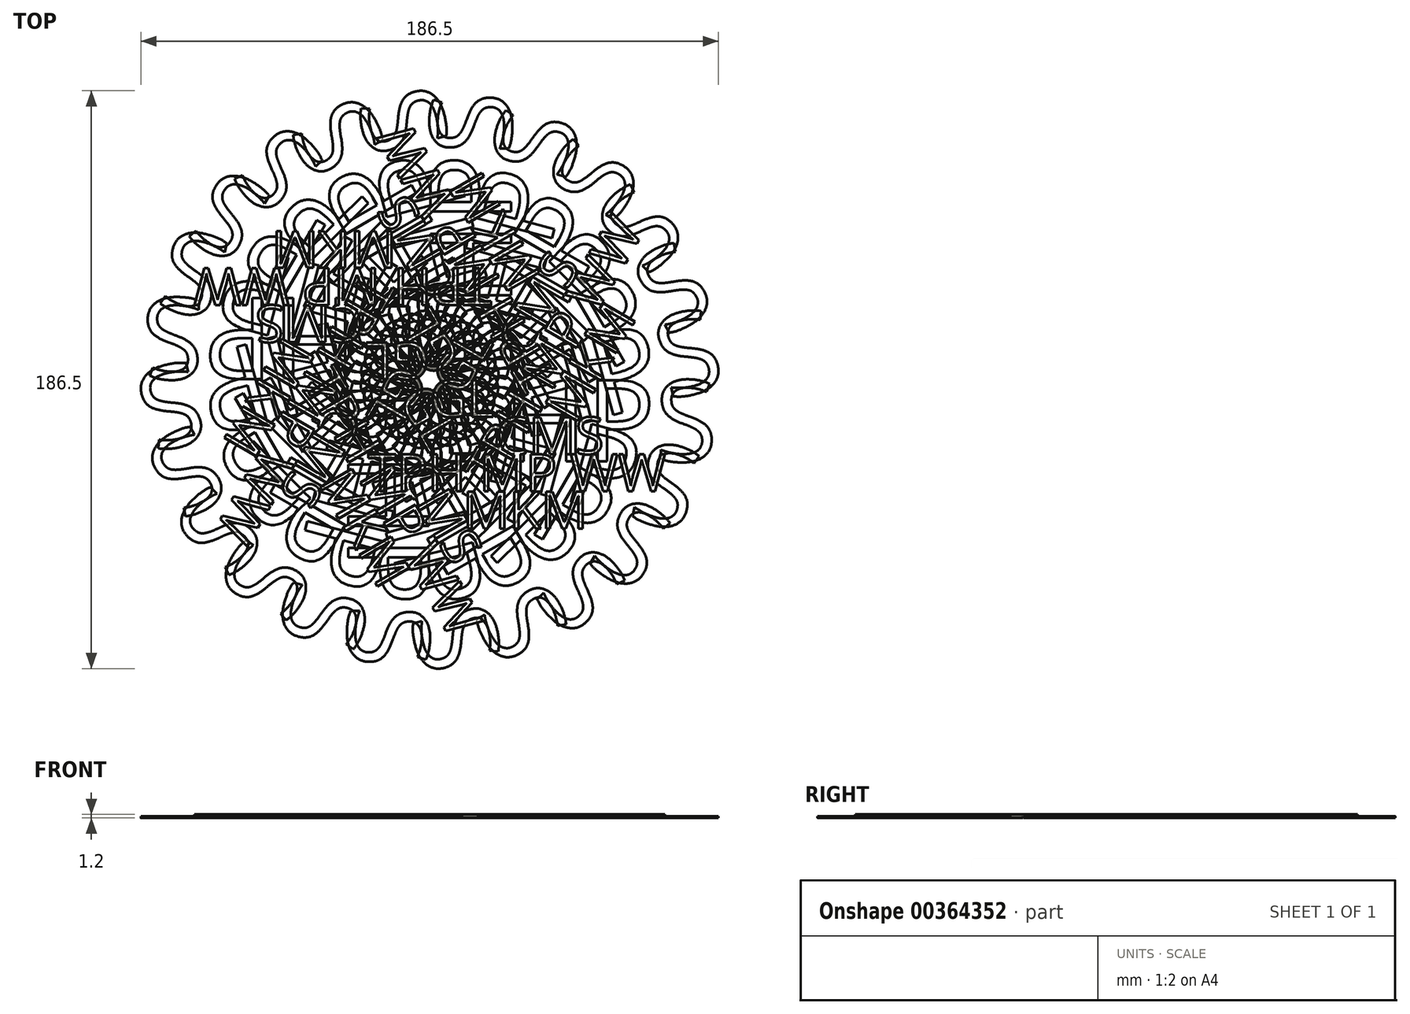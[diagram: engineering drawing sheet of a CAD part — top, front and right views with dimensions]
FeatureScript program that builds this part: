
annotation { "Feature Type Name" : "Feature", "Feature Type Description" : "" }
export const myFeature = defineFeature(function(context is Context, id is Id, definition is map)
    precondition{}
    {
        {
            var Q0;
            Q0=qCreatedBy(makeId("Top.planeOp"),FACE);
            var sketch = newSketch(context, id + "F0", { "sketchPlane" : qUnion([Q0])});
            skText(sketch, "E0", { "text": "GL", "fontName": "OpenSans-Regular.ttf"});
            skText(sketch, "E1", { "text": "CMS", "fontName": "OpenSans-Regular.ttf"});
            skText(sketch, "E2", { "text": "TPH MP WW", "fontName": "OpenSans-Regular.ttf"});
            skText(sketch, "E3", { "text": "MKM", "fontName": "OpenSans-Regular.ttf"});
            const initialGuessF0  = {"E0": [0, -0.012, 1, 0, 0.012], "E1": [0.02148, -0.024, 1, 0, 0.012], "E2": [-0.01992, -0.036, 1, 0, 0.012], "E3": [0.01068, -0.048, 1, 0, 0.012]};
            skSetInitialGuess(sketch, initialGuessF0);
            skSolve(sketch);
        }
        {
            var Q0;
            Q0 = qSketchRegion(id + "F0", true);
            extrude(context, id + "F1", {"entities" : qUnion([Q0]), "depth" : 1.2 * mm});
        }
        {
            var Q0;
            Q0=qCreatedBy(makeId("Front.planeOp"),FACE);
            var sketch = newSketch(context, id + "F2", { "sketchPlane" : qUnion([Q0])});
            skLineSegment(sketch, "E4", {"start": v(0, 0) * mm, "end": v(0, 31.4) * mm, "construction": true});
            skSolve(sketch);
        }
        {
            var Q0;
            Q0=makeQuery(id+"F1.opExtrude","SWEPT_BODY",BODY,{"disambiguationData":[OSD([sQuery(id+"F0.wireOp",EDGE,"E0.sketch_text.stroke-0"),sQuery(id+"F0.wireOp",EDGE,"E0.sketch_text.stroke-1"),sQuery(id+"F0.wireOp",EDGE,"E0.sketch_text.stroke-2"),sQuery(id+"F0.wireOp",EDGE,"E0.sketch_text.stroke-3"),sQuery(id+"F0.wireOp",EDGE,"E0.sketch_text.stroke-4"),sQuery(id+"F0.wireOp",EDGE,"E0.sketch_text.stroke-5"),sQuery(id+"F0.wireOp",EDGE,"E0.sketch_text.stroke-6"),sQuery(id+"F0.wireOp",EDGE,"E0.sketch_text.stroke-7"),sQuery(id+"F0.wireOp",EDGE,"E0.sketch_text.stroke-8"),sQuery(id+"F0.wireOp",EDGE,"E0.sketch_text.stroke-9"),sQuery(id+"F0.wireOp",EDGE,"E0.sketch_text.stroke-10"),sQuery(id+"F0.wireOp",EDGE,"E0.sketch_text.stroke-11"),sQuery(id+"F0.wireOp",EDGE,"E0.sketch_text.stroke-12"),sQuery(id+"F0.wireOp",EDGE,"E0.sketch_text.stroke-13"),sQuery(id+"F0.wireOp",EDGE,"E0.sketch_text.stroke-14"),sQuery(id+"F0.wireOp",EDGE,"E0.sketch_text.stroke-15"),sQuery(id+"F0.wireOp",EDGE,"E0.sketch_text.stroke-16"),sQuery(id+"F0.wireOp",EDGE,"E0.sketch_text.stroke-17"),sQuery(id+"F0.wireOp",EDGE,"E0.sketch_text.stroke-18"),sQuery(id+"F0.wireOp",EDGE,"E0.sketch_text.stroke-19")])]});
            var Q1;
            Q1=makeQuery(id+"F1.opExtrude","SWEPT_BODY",BODY,{"disambiguationData":[OSD([sQuery(id+"F0.wireOp",EDGE,"E1.sketch_text.stroke-0"),sQuery(id+"F0.wireOp",EDGE,"E1.sketch_text.stroke-1"),sQuery(id+"F0.wireOp",EDGE,"E1.sketch_text.stroke-2"),sQuery(id+"F0.wireOp",EDGE,"E1.sketch_text.stroke-3"),sQuery(id+"F0.wireOp",EDGE,"E1.sketch_text.stroke-4"),sQuery(id+"F0.wireOp",EDGE,"E1.sketch_text.stroke-5"),sQuery(id+"F0.wireOp",EDGE,"E1.sketch_text.stroke-6"),sQuery(id+"F0.wireOp",EDGE,"E1.sketch_text.stroke-7"),sQuery(id+"F0.wireOp",EDGE,"E1.sketch_text.stroke-8"),sQuery(id+"F0.wireOp",EDGE,"E1.sketch_text.stroke-9"),sQuery(id+"F0.wireOp",EDGE,"E1.sketch_text.stroke-10"),sQuery(id+"F0.wireOp",EDGE,"E1.sketch_text.stroke-11"),sQuery(id+"F0.wireOp",EDGE,"E1.sketch_text.stroke-12"),sQuery(id+"F0.wireOp",EDGE,"E1.sketch_text.stroke-13"),sQuery(id+"F0.wireOp",EDGE,"E1.sketch_text.stroke-14"),sQuery(id+"F0.wireOp",EDGE,"E2.sketch_text.stroke-35"),sQuery(id+"F0.wireOp",EDGE,"E2.sketch_text.stroke-36"),sQuery(id+"F0.wireOp",EDGE,"E2.sketch_text.stroke-37"),sQuery(id+"F0.wireOp",EDGE,"E2.sketch_text.stroke-38"),sQuery(id+"F0.wireOp",EDGE,"E2.sketch_text.stroke-39"),sQuery(id+"F0.wireOp",EDGE,"E2.sketch_text.stroke-40"),sQuery(id+"F0.wireOp",EDGE,"E2.sketch_text.stroke-41"),sQuery(id+"F0.wireOp",EDGE,"E2.sketch_text.stroke-42"),sQuery(id+"F0.wireOp",EDGE,"E2.sketch_text.stroke-43"),sQuery(id+"F0.wireOp",EDGE,"E2.sketch_text.stroke-44"),sQuery(id+"F0.wireOp",EDGE,"E2.sketch_text.stroke-45"),sQuery(id+"F0.wireOp",EDGE,"E2.sketch_text.stroke-46"),sQuery(id+"F0.wireOp",EDGE,"E2.sketch_text.stroke-47"),sQuery(id+"F0.wireOp",EDGE,"E2.sketch_text.stroke-48"),sQuery(id+"F0.wireOp",EDGE,"E2.sketch_text.stroke-49"),sQuery(id+"F0.wireOp",EDGE,"E2.sketch_text.stroke-50"),sQuery(id+"F0.wireOp",EDGE,"E2.sketch_text.stroke-51"),sQuery(id+"F0.wireOp",EDGE,"E2.sketch_text.stroke-52")])]});
            var Q2;
            Q2=makeQuery(id+"F1.opExtrude","SWEPT_BODY",BODY,{"disambiguationData":[OSD([sQuery(id+"F0.wireOp",EDGE,"E0.sketch_text.stroke-20"),sQuery(id+"F0.wireOp",EDGE,"E0.sketch_text.stroke-21"),sQuery(id+"F0.wireOp",EDGE,"E0.sketch_text.stroke-22"),sQuery(id+"F0.wireOp",EDGE,"E0.sketch_text.stroke-23"),sQuery(id+"F0.wireOp",EDGE,"E0.sketch_text.stroke-24"),sQuery(id+"F0.wireOp",EDGE,"E0.sketch_text.stroke-25")])]});
            var Q3;
            Q3=makeQuery(id+"F1.opExtrude","SWEPT_BODY",BODY,{"disambiguationData":[OSD([sQuery(id+"F0.wireOp",EDGE,"E1.sketch_text.stroke-15"),sQuery(id+"F0.wireOp",EDGE,"E1.sketch_text.stroke-16"),sQuery(id+"F0.wireOp",EDGE,"E1.sketch_text.stroke-17"),sQuery(id+"F0.wireOp",EDGE,"E1.sketch_text.stroke-18"),sQuery(id+"F0.wireOp",EDGE,"E1.sketch_text.stroke-19"),sQuery(id+"F0.wireOp",EDGE,"E1.sketch_text.stroke-20"),sQuery(id+"F0.wireOp",EDGE,"E1.sketch_text.stroke-21"),sQuery(id+"F0.wireOp",EDGE,"E1.sketch_text.stroke-22"),sQuery(id+"F0.wireOp",EDGE,"E1.sketch_text.stroke-23"),sQuery(id+"F0.wireOp",EDGE,"E1.sketch_text.stroke-24"),sQuery(id+"F0.wireOp",EDGE,"E1.sketch_text.stroke-25"),sQuery(id+"F0.wireOp",EDGE,"E1.sketch_text.stroke-26"),sQuery(id+"F0.wireOp",EDGE,"E1.sketch_text.stroke-27"),sQuery(id+"F0.wireOp",EDGE,"E1.sketch_text.stroke-28"),sQuery(id+"F0.wireOp",EDGE,"E1.sketch_text.stroke-29"),sQuery(id+"F0.wireOp",EDGE,"E1.sketch_text.stroke-30"),sQuery(id+"F0.wireOp",EDGE,"E1.sketch_text.stroke-31"),sQuery(id+"F0.wireOp",EDGE,"E1.sketch_text.stroke-32")])]});
            var Q4;
            Q4=makeQuery(id+"F1.opExtrude","SWEPT_BODY",BODY,{"disambiguationData":[OSD([sQuery(id+"F0.wireOp",EDGE,"E2.sketch_text.stroke-0"),sQuery(id+"F0.wireOp",EDGE,"E2.sketch_text.stroke-1"),sQuery(id+"F0.wireOp",EDGE,"E2.sketch_text.stroke-2"),sQuery(id+"F0.wireOp",EDGE,"E2.sketch_text.stroke-3"),sQuery(id+"F0.wireOp",EDGE,"E2.sketch_text.stroke-4"),sQuery(id+"F0.wireOp",EDGE,"E2.sketch_text.stroke-5"),sQuery(id+"F0.wireOp",EDGE,"E2.sketch_text.stroke-6"),sQuery(id+"F0.wireOp",EDGE,"E2.sketch_text.stroke-7")])]});
            var Q5;
            Q5=makeQuery(id+"F1.opExtrude","SWEPT_BODY",BODY,{"disambiguationData":[OSD([sQuery(id+"F0.wireOp",EDGE,"E1.sketch_text.stroke-33"),sQuery(id+"F0.wireOp",EDGE,"E1.sketch_text.stroke-34"),sQuery(id+"F0.wireOp",EDGE,"E1.sketch_text.stroke-35"),sQuery(id+"F0.wireOp",EDGE,"E1.sketch_text.stroke-36"),sQuery(id+"F0.wireOp",EDGE,"E1.sketch_text.stroke-37"),sQuery(id+"F0.wireOp",EDGE,"E1.sketch_text.stroke-38"),sQuery(id+"F0.wireOp",EDGE,"E1.sketch_text.stroke-39"),sQuery(id+"F0.wireOp",EDGE,"E1.sketch_text.stroke-40"),sQuery(id+"F0.wireOp",EDGE,"E1.sketch_text.stroke-41"),sQuery(id+"F0.wireOp",EDGE,"E1.sketch_text.stroke-42"),sQuery(id+"F0.wireOp",EDGE,"E1.sketch_text.stroke-43"),sQuery(id+"F0.wireOp",EDGE,"E1.sketch_text.stroke-44"),sQuery(id+"F0.wireOp",EDGE,"E1.sketch_text.stroke-45"),sQuery(id+"F0.wireOp",EDGE,"E1.sketch_text.stroke-46"),sQuery(id+"F0.wireOp",EDGE,"E1.sketch_text.stroke-47"),sQuery(id+"F0.wireOp",EDGE,"E1.sketch_text.stroke-48"),sQuery(id+"F0.wireOp",EDGE,"E1.sketch_text.stroke-49"),sQuery(id+"F0.wireOp",EDGE,"E1.sketch_text.stroke-50"),sQuery(id+"F0.wireOp",EDGE,"E1.sketch_text.stroke-51"),sQuery(id+"F0.wireOp",EDGE,"E1.sketch_text.stroke-52"),sQuery(id+"F0.wireOp",EDGE,"E1.sketch_text.stroke-53"),sQuery(id+"F0.wireOp",EDGE,"E1.sketch_text.stroke-54"),sQuery(id+"F0.wireOp",EDGE,"E1.sketch_text.stroke-55"),sQuery(id+"F0.wireOp",EDGE,"E1.sketch_text.stroke-56"),sQuery(id+"F0.wireOp",EDGE,"E1.sketch_text.stroke-57")])]});
            var Q6;
            Q6=makeQuery(id+"F1.opExtrude","SWEPT_BODY",BODY,{"disambiguationData":[OSD([sQuery(id+"F0.wireOp",EDGE,"E2.sketch_text.stroke-8"),sQuery(id+"F0.wireOp",EDGE,"E2.sketch_text.stroke-9"),sQuery(id+"F0.wireOp",EDGE,"E2.sketch_text.stroke-10"),sQuery(id+"F0.wireOp",EDGE,"E2.sketch_text.stroke-11"),sQuery(id+"F0.wireOp",EDGE,"E2.sketch_text.stroke-12"),sQuery(id+"F0.wireOp",EDGE,"E2.sketch_text.stroke-13"),sQuery(id+"F0.wireOp",EDGE,"E2.sketch_text.stroke-14"),sQuery(id+"F0.wireOp",EDGE,"E2.sketch_text.stroke-15"),sQuery(id+"F0.wireOp",EDGE,"E2.sketch_text.stroke-16"),sQuery(id+"F0.wireOp",EDGE,"E2.sketch_text.stroke-17"),sQuery(id+"F0.wireOp",EDGE,"E2.sketch_text.stroke-18"),sQuery(id+"F0.wireOp",EDGE,"E2.sketch_text.stroke-19"),sQuery(id+"F0.wireOp",EDGE,"E2.sketch_text.stroke-20"),sQuery(id+"F0.wireOp",EDGE,"E2.sketch_text.stroke-21"),sQuery(id+"F0.wireOp",EDGE,"E2.sketch_text.stroke-22")])]});
            var Q7;
            Q7=makeQuery(id+"F1.opExtrude","SWEPT_BODY",BODY,{"disambiguationData":[OSD([sQuery(id+"F0.wireOp",EDGE,"E2.sketch_text.stroke-23"),sQuery(id+"F0.wireOp",EDGE,"E2.sketch_text.stroke-24"),sQuery(id+"F0.wireOp",EDGE,"E2.sketch_text.stroke-25"),sQuery(id+"F0.wireOp",EDGE,"E2.sketch_text.stroke-26"),sQuery(id+"F0.wireOp",EDGE,"E2.sketch_text.stroke-27"),sQuery(id+"F0.wireOp",EDGE,"E2.sketch_text.stroke-28"),sQuery(id+"F0.wireOp",EDGE,"E2.sketch_text.stroke-29"),sQuery(id+"F0.wireOp",EDGE,"E2.sketch_text.stroke-30"),sQuery(id+"F0.wireOp",EDGE,"E2.sketch_text.stroke-31"),sQuery(id+"F0.wireOp",EDGE,"E2.sketch_text.stroke-32"),sQuery(id+"F0.wireOp",EDGE,"E2.sketch_text.stroke-33"),sQuery(id+"F0.wireOp",EDGE,"E2.sketch_text.stroke-34")])]});
            var Q8;
            Q8=makeQuery(id+"F1.opExtrude","SWEPT_BODY",BODY,{"disambiguationData":[OSD([sQuery(id+"F0.wireOp",EDGE,"E2.sketch_text.stroke-53"),sQuery(id+"F0.wireOp",EDGE,"E2.sketch_text.stroke-54"),sQuery(id+"F0.wireOp",EDGE,"E2.sketch_text.stroke-55"),sQuery(id+"F0.wireOp",EDGE,"E2.sketch_text.stroke-56"),sQuery(id+"F0.wireOp",EDGE,"E2.sketch_text.stroke-57"),sQuery(id+"F0.wireOp",EDGE,"E2.sketch_text.stroke-58"),sQuery(id+"F0.wireOp",EDGE,"E2.sketch_text.stroke-59"),sQuery(id+"F0.wireOp",EDGE,"E2.sketch_text.stroke-60"),sQuery(id+"F0.wireOp",EDGE,"E2.sketch_text.stroke-61"),sQuery(id+"F0.wireOp",EDGE,"E2.sketch_text.stroke-62"),sQuery(id+"F0.wireOp",EDGE,"E2.sketch_text.stroke-63"),sQuery(id+"F0.wireOp",EDGE,"E2.sketch_text.stroke-64"),sQuery(id+"F0.wireOp",EDGE,"E2.sketch_text.stroke-65"),sQuery(id+"F0.wireOp",EDGE,"E2.sketch_text.stroke-66"),sQuery(id+"F0.wireOp",EDGE,"E2.sketch_text.stroke-67")])]});
            var Q9;
            Q9=makeQuery(id+"F1.opExtrude","SWEPT_BODY",BODY,{"disambiguationData":[OSD([sQuery(id+"F0.wireOp",EDGE,"E3.sketch_text.stroke-18"),sQuery(id+"F0.wireOp",EDGE,"E3.sketch_text.stroke-19"),sQuery(id+"F0.wireOp",EDGE,"E3.sketch_text.stroke-20"),sQuery(id+"F0.wireOp",EDGE,"E3.sketch_text.stroke-21"),sQuery(id+"F0.wireOp",EDGE,"E3.sketch_text.stroke-22"),sQuery(id+"F0.wireOp",EDGE,"E3.sketch_text.stroke-23"),sQuery(id+"F0.wireOp",EDGE,"E3.sketch_text.stroke-24"),sQuery(id+"F0.wireOp",EDGE,"E3.sketch_text.stroke-25"),sQuery(id+"F0.wireOp",EDGE,"E3.sketch_text.stroke-26"),sQuery(id+"F0.wireOp",EDGE,"E3.sketch_text.stroke-27"),sQuery(id+"F0.wireOp",EDGE,"E3.sketch_text.stroke-28"),sQuery(id+"F0.wireOp",EDGE,"E3.sketch_text.stroke-29")])]});
            var Q10;
            Q10=makeQuery(id+"F1.opExtrude","SWEPT_BODY",BODY,{"disambiguationData":[OSD([sQuery(id+"F0.wireOp",EDGE,"E3.sketch_text.stroke-0"),sQuery(id+"F0.wireOp",EDGE,"E3.sketch_text.stroke-1"),sQuery(id+"F0.wireOp",EDGE,"E3.sketch_text.stroke-2"),sQuery(id+"F0.wireOp",EDGE,"E3.sketch_text.stroke-3"),sQuery(id+"F0.wireOp",EDGE,"E3.sketch_text.stroke-4"),sQuery(id+"F0.wireOp",EDGE,"E3.sketch_text.stroke-5"),sQuery(id+"F0.wireOp",EDGE,"E3.sketch_text.stroke-6"),sQuery(id+"F0.wireOp",EDGE,"E3.sketch_text.stroke-7"),sQuery(id+"F0.wireOp",EDGE,"E3.sketch_text.stroke-8"),sQuery(id+"F0.wireOp",EDGE,"E3.sketch_text.stroke-9"),sQuery(id+"F0.wireOp",EDGE,"E3.sketch_text.stroke-10"),sQuery(id+"F0.wireOp",EDGE,"E3.sketch_text.stroke-11"),sQuery(id+"F0.wireOp",EDGE,"E3.sketch_text.stroke-12"),sQuery(id+"F0.wireOp",EDGE,"E3.sketch_text.stroke-13"),sQuery(id+"F0.wireOp",EDGE,"E3.sketch_text.stroke-14"),sQuery(id+"F0.wireOp",EDGE,"E3.sketch_text.stroke-15"),sQuery(id+"F0.wireOp",EDGE,"E3.sketch_text.stroke-16"),sQuery(id+"F0.wireOp",EDGE,"E3.sketch_text.stroke-17")])]});
            var Q11;
            Q11=makeQuery(id+"F1.opExtrude","SWEPT_BODY",BODY,{"disambiguationData":[OSD([sQuery(id+"F0.wireOp",EDGE,"E2.sketch_text.stroke-88"),sQuery(id+"F0.wireOp",EDGE,"E2.sketch_text.stroke-89"),sQuery(id+"F0.wireOp",EDGE,"E2.sketch_text.stroke-90"),sQuery(id+"F0.wireOp",EDGE,"E2.sketch_text.stroke-91"),sQuery(id+"F0.wireOp",EDGE,"E2.sketch_text.stroke-92"),sQuery(id+"F0.wireOp",EDGE,"E2.sketch_text.stroke-93"),sQuery(id+"F0.wireOp",EDGE,"E2.sketch_text.stroke-94"),sQuery(id+"F0.wireOp",EDGE,"E2.sketch_text.stroke-95"),sQuery(id+"F0.wireOp",EDGE,"E2.sketch_text.stroke-96"),sQuery(id+"F0.wireOp",EDGE,"E2.sketch_text.stroke-97"),sQuery(id+"F0.wireOp",EDGE,"E2.sketch_text.stroke-98"),sQuery(id+"F0.wireOp",EDGE,"E2.sketch_text.stroke-99"),sQuery(id+"F0.wireOp",EDGE,"E2.sketch_text.stroke-100"),sQuery(id+"F0.wireOp",EDGE,"E2.sketch_text.stroke-101"),sQuery(id+"F0.wireOp",EDGE,"E2.sketch_text.stroke-102"),sQuery(id+"F0.wireOp",EDGE,"E2.sketch_text.stroke-103"),sQuery(id+"F0.wireOp",EDGE,"E2.sketch_text.stroke-104"),sQuery(id+"F0.wireOp",EDGE,"E2.sketch_text.stroke-105"),sQuery(id+"F0.wireOp",EDGE,"E2.sketch_text.stroke-106"),sQuery(id+"F0.wireOp",EDGE,"E2.sketch_text.stroke-107")])]});
            var Q12;
            Q12=makeQuery(id+"F1.opExtrude","SWEPT_BODY",BODY,{"disambiguationData":[OSD([sQuery(id+"F0.wireOp",EDGE,"E2.sketch_text.stroke-68"),sQuery(id+"F0.wireOp",EDGE,"E2.sketch_text.stroke-69"),sQuery(id+"F0.wireOp",EDGE,"E2.sketch_text.stroke-70"),sQuery(id+"F0.wireOp",EDGE,"E2.sketch_text.stroke-71"),sQuery(id+"F0.wireOp",EDGE,"E2.sketch_text.stroke-72"),sQuery(id+"F0.wireOp",EDGE,"E2.sketch_text.stroke-73"),sQuery(id+"F0.wireOp",EDGE,"E2.sketch_text.stroke-74"),sQuery(id+"F0.wireOp",EDGE,"E2.sketch_text.stroke-75"),sQuery(id+"F0.wireOp",EDGE,"E2.sketch_text.stroke-76"),sQuery(id+"F0.wireOp",EDGE,"E2.sketch_text.stroke-77"),sQuery(id+"F0.wireOp",EDGE,"E2.sketch_text.stroke-78"),sQuery(id+"F0.wireOp",EDGE,"E2.sketch_text.stroke-79"),sQuery(id+"F0.wireOp",EDGE,"E2.sketch_text.stroke-80"),sQuery(id+"F0.wireOp",EDGE,"E2.sketch_text.stroke-81"),sQuery(id+"F0.wireOp",EDGE,"E2.sketch_text.stroke-82"),sQuery(id+"F0.wireOp",EDGE,"E2.sketch_text.stroke-83"),sQuery(id+"F0.wireOp",EDGE,"E2.sketch_text.stroke-84"),sQuery(id+"F0.wireOp",EDGE,"E2.sketch_text.stroke-85"),sQuery(id+"F0.wireOp",EDGE,"E2.sketch_text.stroke-86"),sQuery(id+"F0.wireOp",EDGE,"E2.sketch_text.stroke-87")])]});
            var Q13;
            Q13=makeQuery(id+"F1.opExtrude","SWEPT_BODY",BODY,{"disambiguationData":[OSD([sQuery(id+"F0.wireOp",EDGE,"E3.sketch_text.stroke-30"),sQuery(id+"F0.wireOp",EDGE,"E3.sketch_text.stroke-31"),sQuery(id+"F0.wireOp",EDGE,"E3.sketch_text.stroke-32"),sQuery(id+"F0.wireOp",EDGE,"E3.sketch_text.stroke-33"),sQuery(id+"F0.wireOp",EDGE,"E3.sketch_text.stroke-34"),sQuery(id+"F0.wireOp",EDGE,"E3.sketch_text.stroke-35"),sQuery(id+"F0.wireOp",EDGE,"E3.sketch_text.stroke-36"),sQuery(id+"F0.wireOp",EDGE,"E3.sketch_text.stroke-37"),sQuery(id+"F0.wireOp",EDGE,"E3.sketch_text.stroke-38"),sQuery(id+"F0.wireOp",EDGE,"E3.sketch_text.stroke-39"),sQuery(id+"F0.wireOp",EDGE,"E3.sketch_text.stroke-40"),sQuery(id+"F0.wireOp",EDGE,"E3.sketch_text.stroke-41"),sQuery(id+"F0.wireOp",EDGE,"E3.sketch_text.stroke-42"),sQuery(id+"F0.wireOp",EDGE,"E3.sketch_text.stroke-43"),sQuery(id+"F0.wireOp",EDGE,"E3.sketch_text.stroke-44"),sQuery(id+"F0.wireOp",EDGE,"E3.sketch_text.stroke-45"),sQuery(id+"F0.wireOp",EDGE,"E3.sketch_text.stroke-46"),sQuery(id+"F0.wireOp",EDGE,"E3.sketch_text.stroke-47")])]});
            var Q14;
            Q14=sQuery(id+"F2.wireOp",EDGE,"E4");
            circularPattern(context, id + "F3", {"entities" : qUnion([Q0, Q1, Q2, Q3, Q4, Q5, Q6, Q7, Q8, Q9, Q10, Q11, Q12, Q13]), "axis" : qUnion([Q14]), "angle" : 360 * degree, "instanceCount" : 6, "oppositeDirection" : true, "equalSpace" : true});
        }
        {
            var Q0;
            Q0=qCreatedBy(makeId("Top.planeOp"),FACE);
            var sketch = newSketch(context, id + "F4", { "sketchPlane" : qUnion([Q0])});
            skText(sketch, "E5", { "text": "BHPS", "fontName": "OpenSans-Regular.ttf"});
            const initialGuessF4  = {"E5": [0, -0.02634, 1, 0, 0.02634]};
            skSetInitialGuess(sketch, initialGuessF4);
            skSolve(sketch);
        }
        {
            var Q0;
            Q0 = qSketchRegion(id + "F4", true);
            extrude(context, id + "F5", {"entities" : qUnion([Q0]), "depth" : .6 * mm});
        }
        {
            var Q0;
            Q0=makeQuery(id+"F5.opExtrude","SWEPT_BODY",BODY,{"disambiguationData":[OSD([sQuery(id+"F4.wireOp",EDGE,"E5.sketch_text.stroke-0"),sQuery(id+"F4.wireOp",EDGE,"E5.sketch_text.stroke-1"),sQuery(id+"F4.wireOp",EDGE,"E5.sketch_text.stroke-2"),sQuery(id+"F4.wireOp",EDGE,"E5.sketch_text.stroke-3"),sQuery(id+"F4.wireOp",EDGE,"E5.sketch_text.stroke-4"),sQuery(id+"F4.wireOp",EDGE,"E5.sketch_text.stroke-5"),sQuery(id+"F4.wireOp",EDGE,"E5.sketch_text.stroke-6"),sQuery(id+"F4.wireOp",EDGE,"E5.sketch_text.stroke-7"),sQuery(id+"F4.wireOp",EDGE,"E5.sketch_text.stroke-8"),sQuery(id+"F4.wireOp",EDGE,"E5.sketch_text.stroke-9"),sQuery(id+"F4.wireOp",EDGE,"E5.sketch_text.stroke-10"),sQuery(id+"F4.wireOp",EDGE,"E5.sketch_text.stroke-11"),sQuery(id+"F4.wireOp",EDGE,"E5.sketch_text.stroke-12"),sQuery(id+"F4.wireOp",EDGE,"E5.sketch_text.stroke-13"),sQuery(id+"F4.wireOp",EDGE,"E5.sketch_text.stroke-14"),sQuery(id+"F4.wireOp",EDGE,"E5.sketch_text.stroke-15"),sQuery(id+"F4.wireOp",EDGE,"E5.sketch_text.stroke-16"),sQuery(id+"F4.wireOp",EDGE,"E5.sketch_text.stroke-17"),sQuery(id+"F4.wireOp",EDGE,"E5.sketch_text.stroke-18"),sQuery(id+"F4.wireOp",EDGE,"E5.sketch_text.stroke-19"),sQuery(id+"F4.wireOp",EDGE,"E5.sketch_text.stroke-20"),sQuery(id+"F4.wireOp",EDGE,"E5.sketch_text.stroke-21"),sQuery(id+"F4.wireOp",EDGE,"E5.sketch_text.stroke-22"),sQuery(id+"F4.wireOp",EDGE,"E5.sketch_text.stroke-23"),sQuery(id+"F4.wireOp",EDGE,"E5.sketch_text.stroke-24")])]});
            var Q1;
            Q1=makeQuery(id+"F5.opExtrude","SWEPT_BODY",BODY,{"disambiguationData":[OSD([sQuery(id+"F4.wireOp",EDGE,"E5.sketch_text.stroke-25"),sQuery(id+"F4.wireOp",EDGE,"E5.sketch_text.stroke-26"),sQuery(id+"F4.wireOp",EDGE,"E5.sketch_text.stroke-27"),sQuery(id+"F4.wireOp",EDGE,"E5.sketch_text.stroke-28"),sQuery(id+"F4.wireOp",EDGE,"E5.sketch_text.stroke-29"),sQuery(id+"F4.wireOp",EDGE,"E5.sketch_text.stroke-30"),sQuery(id+"F4.wireOp",EDGE,"E5.sketch_text.stroke-31"),sQuery(id+"F4.wireOp",EDGE,"E5.sketch_text.stroke-32"),sQuery(id+"F4.wireOp",EDGE,"E5.sketch_text.stroke-33"),sQuery(id+"F4.wireOp",EDGE,"E5.sketch_text.stroke-34"),sQuery(id+"F4.wireOp",EDGE,"E5.sketch_text.stroke-35"),sQuery(id+"F4.wireOp",EDGE,"E5.sketch_text.stroke-36")])]});
            var Q2;
            Q2=makeQuery(id+"F5.opExtrude","SWEPT_BODY",BODY,{"disambiguationData":[OSD([sQuery(id+"F4.wireOp",EDGE,"E5.sketch_text.stroke-37"),sQuery(id+"F4.wireOp",EDGE,"E5.sketch_text.stroke-38"),sQuery(id+"F4.wireOp",EDGE,"E5.sketch_text.stroke-39"),sQuery(id+"F4.wireOp",EDGE,"E5.sketch_text.stroke-40"),sQuery(id+"F4.wireOp",EDGE,"E5.sketch_text.stroke-41"),sQuery(id+"F4.wireOp",EDGE,"E5.sketch_text.stroke-42"),sQuery(id+"F4.wireOp",EDGE,"E5.sketch_text.stroke-43"),sQuery(id+"F4.wireOp",EDGE,"E5.sketch_text.stroke-44"),sQuery(id+"F4.wireOp",EDGE,"E5.sketch_text.stroke-45"),sQuery(id+"F4.wireOp",EDGE,"E5.sketch_text.stroke-46"),sQuery(id+"F4.wireOp",EDGE,"E5.sketch_text.stroke-47"),sQuery(id+"F4.wireOp",EDGE,"E5.sketch_text.stroke-48"),sQuery(id+"F4.wireOp",EDGE,"E5.sketch_text.stroke-49"),sQuery(id+"F4.wireOp",EDGE,"E5.sketch_text.stroke-50"),sQuery(id+"F4.wireOp",EDGE,"E5.sketch_text.stroke-51")])]});
            var Q3;
            Q3=makeQuery(id+"F5.opExtrude","SWEPT_BODY",BODY,{"disambiguationData":[OSD([sQuery(id+"F4.wireOp",EDGE,"E5.sketch_text.stroke-52"),sQuery(id+"F4.wireOp",EDGE,"E5.sketch_text.stroke-53"),sQuery(id+"F4.wireOp",EDGE,"E5.sketch_text.stroke-54"),sQuery(id+"F4.wireOp",EDGE,"E5.sketch_text.stroke-55"),sQuery(id+"F4.wireOp",EDGE,"E5.sketch_text.stroke-56"),sQuery(id+"F4.wireOp",EDGE,"E5.sketch_text.stroke-57"),sQuery(id+"F4.wireOp",EDGE,"E5.sketch_text.stroke-58"),sQuery(id+"F4.wireOp",EDGE,"E5.sketch_text.stroke-59"),sQuery(id+"F4.wireOp",EDGE,"E5.sketch_text.stroke-60"),sQuery(id+"F4.wireOp",EDGE,"E5.sketch_text.stroke-61"),sQuery(id+"F4.wireOp",EDGE,"E5.sketch_text.stroke-62"),sQuery(id+"F4.wireOp",EDGE,"E5.sketch_text.stroke-63"),sQuery(id+"F4.wireOp",EDGE,"E5.sketch_text.stroke-64"),sQuery(id+"F4.wireOp",EDGE,"E5.sketch_text.stroke-65"),sQuery(id+"F4.wireOp",EDGE,"E5.sketch_text.stroke-66"),sQuery(id+"F4.wireOp",EDGE,"E5.sketch_text.stroke-67"),sQuery(id+"F4.wireOp",EDGE,"E5.sketch_text.stroke-68"),sQuery(id+"F4.wireOp",EDGE,"E5.sketch_text.stroke-69"),sQuery(id+"F4.wireOp",EDGE,"E5.sketch_text.stroke-70"),sQuery(id+"F4.wireOp",EDGE,"E5.sketch_text.stroke-71"),sQuery(id+"F4.wireOp",EDGE,"E5.sketch_text.stroke-72"),sQuery(id+"F4.wireOp",EDGE,"E5.sketch_text.stroke-73"),sQuery(id+"F4.wireOp",EDGE,"E5.sketch_text.stroke-74"),sQuery(id+"F4.wireOp",EDGE,"E5.sketch_text.stroke-75"),sQuery(id+"F4.wireOp",EDGE,"E5.sketch_text.stroke-76")])]});
            var Q4;
            Q4=sQuery(id+"F2.wireOp",EDGE,"E4");
            circularPattern(context, id + "F6", {"entities" : qUnion([Q0, Q1, Q2, Q3]), "axis" : qUnion([Q4]), "angle" : 360 * degree, "instanceCount" : 24, "equalSpace" : true});
        }
    });
